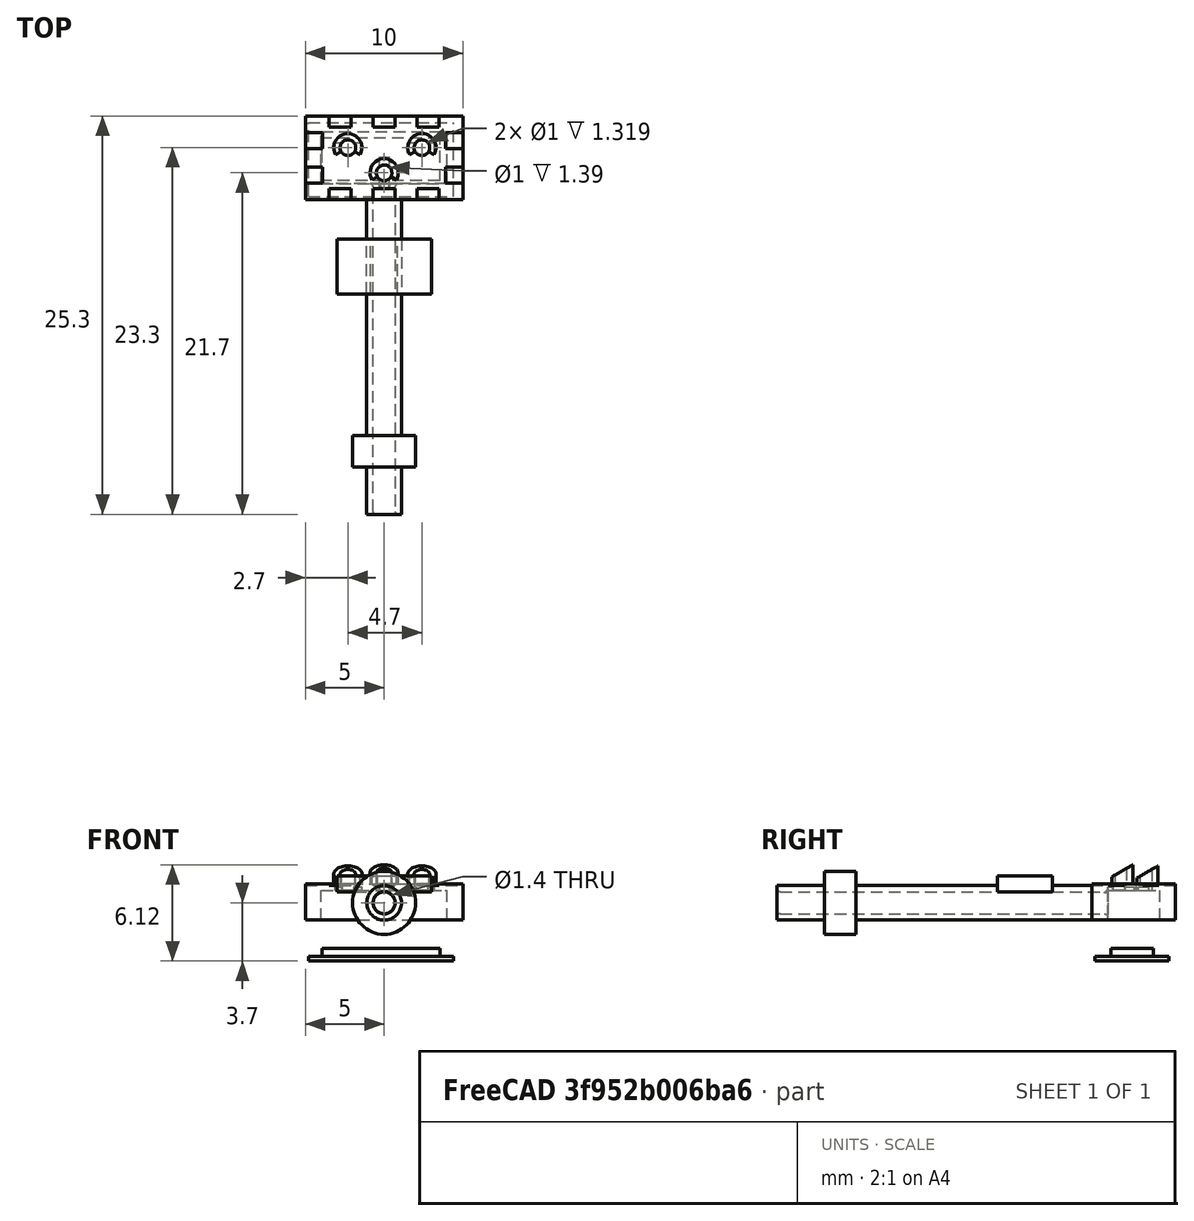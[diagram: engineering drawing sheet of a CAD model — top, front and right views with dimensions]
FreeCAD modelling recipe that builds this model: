
FCSTD DOCUMENT  (FreeCAD 0.20R29177 (Git))
Label: Level crossing warning lights 6
License: All rights reserved
LicenseURL: http://en.wikipedia.org/wiki/All_rights_reserved
objects: PartDesign::SubtractiveBox×7, PartDesign::LinearPattern×6, PartDesign::AdditiveCylinder×5, PartDesign::AdditiveBox×4, PartDesign::SubtractiveCylinder×4, PartDesign::MultiTransform×2, PartDesign::Body×2, PartDesign::Fillet×2
note: 54 computed .brp shape members not serialized (recipe doc carries the construction recipe); baked Part::Feature solids carry a one-line shape summary decoded from their .brp

FEATURE [PartDesign::AdditiveBox] Box
  AttacherType = Attacher::AttachEngine3D
  AttachmentOffset = pos=(-1,-1,-1.2) rot=(0,0,1;0rad)
  Height = 2.3
  Length = 10
  MapMode = 5
  Placement = pos=(-1,-1,-1.2) rot=(0,0,1;0rad)
  Support = -> [XY_Plane]
  Width = 5.3
FEATURE [PartDesign::AdditiveCylinder] Cylinder001
  Angle = 240
  AttacherType = Attacher::AttachEngine3D
  AttachmentOffset = pos=(1.7,2.3,0.5) rot=(0,0,1;-0.523599rad)
  BaseFeature = -> Box
  FirstAngle = 0
  Height = 3
  MapMode = 5
  Placement = pos=(1.7,2.3,0.5) rot=(0,0,1;5.75959rad)
  Radius = 0.9
  SecondAngle = 0
  Support = -> [XY_Plane]
FEATURE [PartDesign::SubtractiveCylinder] Cylinder
  Angle = 360
  AttacherType = Attacher::AttachEngine3D
  AttachmentOffset = pos=(1.7,2.3,-1) rot=(0,0,1;0rad)
  BaseFeature = -> Cylinder001
  FirstAngle = 0
  Height = 4
  MapMode = 5
  Placement = pos=(1.7,2.3,-1) rot=(0,0,1;0rad)
  Radius = 0.5
  SecondAngle = 0
  Support = -> [XY_Plane]
FEATURE [PartDesign::AdditiveCylinder] Cylinder002
  Angle = 240
  AttacherType = Attacher::AttachEngine3D
  AttachmentOffset = pos=(6.4,2.3,0.5) rot=(0,0,1;-0.523599rad)
  BaseFeature = -> Cylinder
  FirstAngle = 0
  Height = 3
  MapMode = 5
  Placement = pos=(6.4,2.3,0.5) rot=(0,0,1;5.75959rad)
  Radius = 0.9
  SecondAngle = 0
  Support = -> [XY_Plane]
FEATURE [PartDesign::SubtractiveCylinder] Cylinder003
  Angle = 360
  AttacherType = Attacher::AttachEngine3D
  AttachmentOffset = pos=(6.4,2.3,-1) rot=(0,0,1;0rad)
  BaseFeature = -> Cylinder002
  FirstAngle = 0
  Height = 4
  MapMode = 5
  Placement = pos=(6.4,2.3,-1) rot=(0,0,1;0rad)
  Radius = 0.5
  SecondAngle = 0
  Support = -> [XY_Plane]
FEATURE [PartDesign::AdditiveCylinder] Cylinder004
  Angle = 240
  AttacherType = Attacher::AttachEngine3D
  AttachmentOffset = pos=(4,0.7,0.5) rot=(0,0,1;-0.523599rad)
  BaseFeature = -> Cylinder003
  FirstAngle = 0
  Height = 3
  MapMode = 5
  Placement = pos=(4,0.7,0.5) rot=(0,0,1;5.75959rad)
  Radius = 0.9
  SecondAngle = 0
  Support = -> [XY_Plane]
FEATURE [PartDesign::SubtractiveCylinder] Cylinder005
  Angle = 360
  AttacherType = Attacher::AttachEngine3D
  AttachmentOffset = pos=(4,0.7,-1) rot=(0,0,1;0rad)
  BaseFeature = -> Cylinder004
  FirstAngle = 0
  Height = 4
  MapMode = 5
  Placement = pos=(4,0.7,-1) rot=(0,0,1;0rad)
  Radius = 0.5
  SecondAngle = 0
  Support = -> [XY_Plane]
FEATURE [PartDesign::AdditiveCylinder] Cylinder009
  Angle = 360
  AttacherType = Attacher::AttachEngine3D
  AttachmentOffset = pos=(4,-0.1,0) rot=(0,0,1;0rad)
  BaseFeature = -> Cylinder005
  FirstAngle = 0
  Height = 21
  MapMode = 5
  Placement = pos=(4,0,-0.1) rot=(1,0,0;1.5708rad)
  Radius = 1.1
  SecondAngle = 0
  Support = -> [XZ_Plane]
FEATURE [PartDesign::AdditiveCylinder] Cylinder006
  Angle = 360
  AttacherType = Attacher::AttachEngine3D
  AttachmentOffset = pos=(4,-0.1,16) rot=(0,0,1;0rad)
  BaseFeature = -> Cylinder009
  FirstAngle = 0
  Height = 2
  MapMode = 5
  Placement = pos=(4,-16,-0.1) rot=(1,0,0;1.5708rad)
  Radius = 2
  SecondAngle = 0
  Support = -> [XZ_Plane]
FEATURE [PartDesign::SubtractiveCylinder] Cylinder007
  Angle = 360
  AttacherType = Attacher::AttachEngine3D
  AttachmentOffset = pos=(4,-0.1,-1) rot=(0,0,1;0rad)
  BaseFeature = -> Cylinder006
  FirstAngle = 0
  Height = 22
  MapMode = 5
  Placement = pos=(4,1,-0.1) rot=(1,0,0;1.5708rad)
  Radius = 0.7
  SecondAngle = 0
  Support = -> [XZ_Plane]
FEATURE [PartDesign::SubtractiveBox] Box003
  AttacherType = Attacher::AttachEngine3D
  AttachmentOffset = pos=(0,0,-1.3) rot=(0,0,1;0rad)
  BaseFeature = -> Cylinder007
  Height = 2
  Length = 8
  MapMode = 5
  Placement = pos=(0,0,-1.3) rot=(0,0,1;0rad)
  Support = -> [XY_Plane]
  Width = 3.3
FEATURE [PartDesign::AdditiveBox] Box004
  AttacherType = Attacher::AttachEngine3D
  AttachmentOffset = pos=(1,-7,0.6) rot=(0,0,1;0rad)
  BaseFeature = -> Box003
  Height = 1
  Length = 6
  MapMode = 5
  Placement = pos=(1,-7,0.6) rot=(0,0,1;0rad)
  Support = -> [XY_Plane]
  Width = 3.5
FEATURE [PartDesign::SubtractiveBox] Box005
  AttacherType = Attacher::AttachEngine3D
  AttachmentOffset = pos=(0.5,-1,1) rot=(0,0,1;0rad)
  BaseFeature = -> Box004
  Height = 0.1
  Length = 1.4
  MapMode = 5
  Placement = pos=(0.5,-1,1) rot=(0,0,1;0rad)
  Support = -> [XY_Plane]
  Width = 0.7
FEATURE [PartDesign::LinearPattern] LinearPattern
  Direction = -> X_Axis
  Length = 5.6
  Occurrences = 3
  Placement = pos=(0.5,-1,1) rot=(0,0,1;0rad)
FEATURE [PartDesign::LinearPattern] LinearPattern001
  Direction = -> Y_Axis
  Length = 4.6
  Occurrences = 2
  Placement = pos=(0.5,-1,1) rot=(0,0,1;0rad)
FEATURE [PartDesign::MultiTransform] MultiTransform
  BaseFeature = -> Box005
  Originals = -> [Box005]
  Placement = pos=(0.5,-1,1) rot=(0,0,1;0rad)
  Transformations = -> [LinearPattern,LinearPattern001]
FEATURE [PartDesign::SubtractiveBox] Box006
  AttacherType = Attacher::AttachEngine3D
  AttachmentOffset = pos=(-1,0.05,1) rot=(-1,0,0;0rad)
  BaseFeature = -> MultiTransform
  Height = 0.2
  Length = 1.1
  MapMode = 5
  Placement = pos=(-1,0.05,1) rot=(0,0,1;0rad)
  Support = -> [XY_Plane]
  Width = 1
FEATURE [PartDesign::LinearPattern] LinearPattern003
  Direction = -> X_Axis
  Length = 8.9
  Occurrences = 2
  Placement = pos=(-1,0.05,1) rot=(0,0,1;0rad)
FEATURE [PartDesign::LinearPattern] LinearPattern004
  Direction = -> Y_Axis
  Length = 2.2
  Occurrences = 2
  Placement = pos=(-1,0.05,1) rot=(0,0,1;0rad)
FEATURE [PartDesign::MultiTransform] MultiTransform001
  BaseFeature = -> Box006
  Originals = -> [Box006]
  Placement = pos=(-1,0.05,1) rot=(0,0,1;0rad)
  Transformations = -> [LinearPattern003,LinearPattern004]
FEATURE [PartDesign::SubtractiveBox] Box007
  AttacherType = Attacher::AttachEngine3D
  AttachmentOffset = pos=(3,-1.5,2.84) rot=(-1,0,0;1.0472rad)
  BaseFeature = -> MultiTransform001
  Height = 3.3
  Length = 2
  MapMode = 5
  Placement = pos=(3,-1.5,2.84) rot=(-1,0,0;1.0472rad)
  Support = -> [XY_Plane]
  Width = 2
FEATURE [PartDesign::SubtractiveBox] Box008
  AttacherType = Attacher::AttachEngine3D
  AttachmentOffset = pos=(0.5,0.5,3) rot=(-1,0,0;1.0472rad)
  BaseFeature = -> Box007
  Height = 3.3
  Length = 2.2
  MapMode = 5
  Placement = pos=(0.5,0.5,3) rot=(-1,0,0;1.0472rad)
  Support = -> [XY_Plane]
  Width = 2
FEATURE [PartDesign::LinearPattern] LinearPattern005
  BaseFeature = -> Box008
  Direction = -> X_Axis
  Length = 5
  Occurrences = 2
  Originals = -> [Box008]
  Placement = pos=(0.5,0.5,3) rot=(-1,0,0;1.0472rad)
FEATURE [PartDesign::SubtractiveBox] Box009
  AttacherType = Attacher::AttachEngine3D
  AttachmentOffset = pos=(0.9,1.95,-0.1) rot=(0,0,1;0rad)
  BaseFeature = -> LinearPattern005
  Height = 1
  Length = 1.7
  MapMode = 5
  Placement = pos=(0.9,1.95,-0.1) rot=(0,0,1;0rad)
  Support = -> [XY_Plane]
  Width = 0.65
FEATURE [PartDesign::LinearPattern] LinearPattern006
  BaseFeature = -> Box009
  Direction = -> X_Axis
  Length = 4.6
  Occurrences = 2
  Originals = -> [Box009]
  Placement = pos=(0.9,1.95,-0.1) rot=(0,0,1;0rad)
FEATURE [PartDesign::SubtractiveBox] Box010
  AttacherType = Attacher::AttachEngine3D
  AttachmentOffset = pos=(3.7,0,0.7) rot=(0,0,1;0rad)
  BaseFeature = -> LinearPattern006
  Height = 0.2
  Length = 0.65
  MapMode = 5
  Placement = pos=(3.7,0,0.7) rot=(0,0,1;0rad)
  Support = -> [XY_Plane]
  Width = 1.7
FEATURE [PartDesign::AdditiveBox] Box011
  AttacherType = Attacher::AttachEngine3D
  AttachmentOffset = pos=(-0.8,-0.8,-3.8) rot=(0,0,1;0rad)
  Height = 0.3
  Length = 9.2
  MapMode = 5
  Placement = pos=(-0.8,-0.8,-3.8) rot=(0,0,1;0rad)
  Support = -> [XY_Plane001]
  Width = 4.7
FEATURE [PartDesign::AdditiveBox] Box012
  AttacherType = Attacher::AttachEngine3D
  AttachmentOffset = pos=(0.05,0.2,-3.6) rot=(0,0,1;0rad)
  BaseFeature = -> Box011
  Height = 0.6
  Length = 7.5
  MapMode = 5
  Placement = pos=(0.05,0.2,-3.6) rot=(0,0,1;0rad)
  Support = -> [XY_Plane001]
  Width = 2.7
FEATURE [PartDesign::Body] Body001
  Group = -> [Box011,Box012]
  Origin = -> Origin001
  Tip = -> Box012
FEATURE [PartDesign::Fillet] Fillet
  Base = -> Box010 [Edge219]
  BaseFeature = -> Box010
  Placement = pos=(3.7,0,0.7) rot=(0,0,1;0rad)
  Radius = 0.2
  SupportTransform = false
  UseAllEdges = false
FEATURE [PartDesign::Fillet] Fillet001
  Base = -> Fillet [Edge128]
  BaseFeature = -> Fillet
  Placement = pos=(3.7,0,0.7) rot=(0,0,1;0rad)
  Radius = 0.2
  SupportTransform = false
  UseAllEdges = false
FEATURE [PartDesign::Body] Body
  Group = -> [Box,Cylinder001,Cylinder,Cylinder002,Cylinder003,Cylinder004,Cylinder005,Cylinder009,Cylinder006,Cylinder007,Box003,Box004,Box005,MultiTransform,LinearPattern,LinearPattern001,Box006,MultiTransform001,LinearPattern003,LinearPattern004,Box007,Box008,LinearPattern005,Box009,LinearPattern006,Box010,Fillet,Fillet001]
  Origin = -> Origin
  Tip = -> Fillet001
